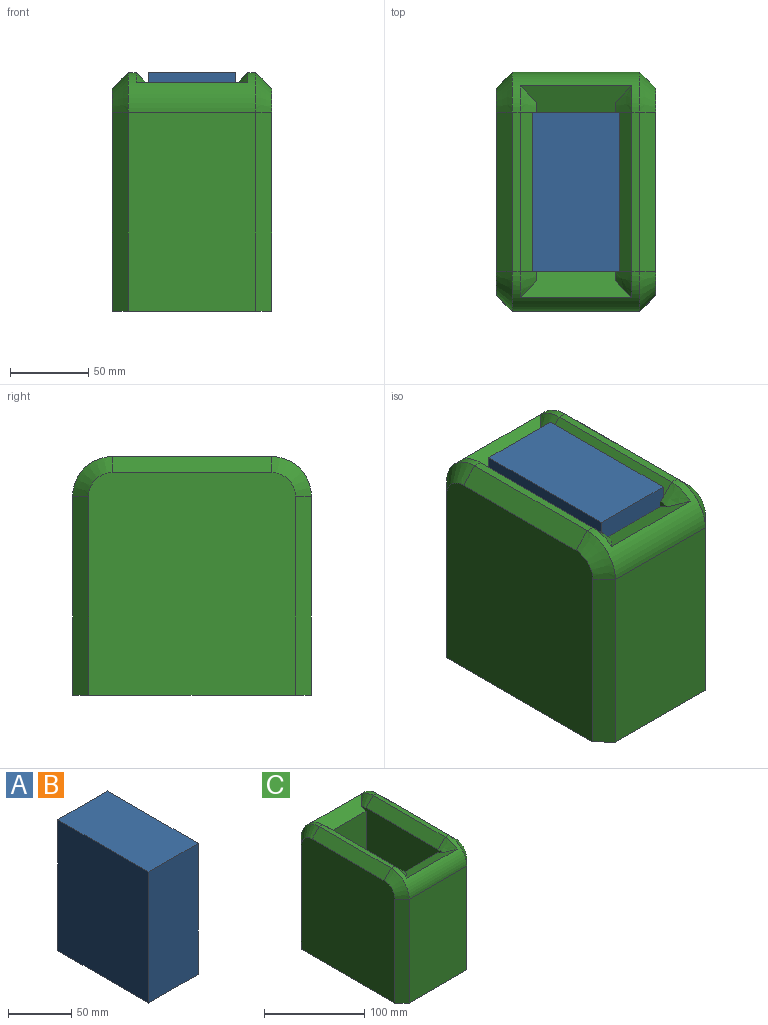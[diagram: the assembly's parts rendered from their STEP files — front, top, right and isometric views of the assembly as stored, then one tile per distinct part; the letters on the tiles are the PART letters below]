
ASSEMBLY  parts=3 mates=1
PART A: 6 faces, bbox 55.7x101.6x127 mm
  f0: plane 127x55.65mm, normal (0,1,0), area 7068mm2, adj f1,f3,f4,f5
  f1: plane 127x101.6mm, normal (-1,0,0), area 12903.2mm2, adj f0,f2,f4,f5
  f2: plane 127x55.65mm, normal (0,-1,0), area 7068mm2, adj f1,f3,f4,f5
  f3: plane 127x101.6mm, normal (1,0,0), area 12903.2mm2, adj f0,f2,f4,f5
  f4: plane 101.6x55.65mm, normal (0,0,1), area 5654.4mm2, adj f0,f1,f2,f3
  f5: plane 101.6x55.65mm, normal (0,0,-1), area 5654.4mm2, adj f0,f1,f2,f3
PART B: same geometry as A
PART C: 32 faces, bbox 101.6x152.4x152.4 mm
  f0: plane 101.6x5.08mm, normal (0,0,1), area 516.1mm2, adj f12,f13,f16,f27
  f1: plane 127x81.28mm, normal (0,1,0), area 10322.6mm2, adj f6,f13,f18,f23
  f2: plane 142.24x132.08mm, normal (-1,0,0), area 18687.4mm2, adj f6,f14,f15,f16,f17,f18
  f3: plane 127x81.28mm, normal (0,-1,0), area 10322.6mm2, adj f6,f12,f14,f19
  f4: plane 142.24x132.08mm, normal (1,0,0), area 18687.4mm2, adj f6,f19,f20,f21,f22,f23
  f5: plane 101.6x5.08mm, normal (0,0,1), area 516.1mm2, adj f12,f13,f21,f28
  f6: plane 152.4x101.6mm, normal (0,0,-1), area 15277.4mm2, adj f1,f2,f3,f4,f14,f18,f19,f23
  f7: plane 116.84x113.52mm, normal (1,0,0), area 11896.6mm2, adj f8,f10,f11,f24,f25,f27,f29,f31
  f8: plane 112.96x50.8mm, normal (0,1,0), area 5738.3mm2, adj f7,f9,f11,f31
  f9: plane 116.84x113.52mm, normal (-1,0,0), area 11896.6mm2, adj f8,f10,f11,f24,f26,f28,f30,f31
  f10: plane 112.96x50.8mm, normal (0,-1,0), area 5738.3mm2, adj f7,f9,f11,f24
  f11: plane 101.6x50.8mm, normal (0,0,1), area 5161.3mm2, adj f7,f8,f9,f10
  f12: cylinder r=25.4mm len=81.28mm, axis (-1,0,0), area 1924.7mm2, adj f0,f3,f5,f15,f20,f29,f30,f31
  f13: cylinder r=25.4mm len=81.28mm, axis (1,0,0), area 1924.7mm2, adj f0,f1,f5,f17,f22,f24,f25,f26
  f14: plane 127x10.16mm, normal (-0.71,-0.71,0), area 1824.8mm2, adj f2,f3,f6,f15
  f15: cone r=15.24mm half-angle=45deg, axis (1,0,0), area 458.6mm2, adj f2,f12,f14,f16
  f16: plane 101.6x10.16mm, normal (-0.71,0,0.71), area 1459.8mm2, adj f0,f2,f15,f17
  f17: cone r=15.24mm half-angle=45deg, axis (1,0,0), area 458.6mm2, adj f2,f13,f16,f18
  f18: plane 127x10.16mm, normal (-0.71,0.71,0), area 1824.8mm2, adj f1,f2,f6,f17
  f19: plane 127x10.16mm, normal (0.71,-0.71,0), area 1824.8mm2, adj f3,f4,f6,f20
  f20: cone r=15.24mm half-angle=45deg, axis (-1,0,0), area 458.6mm2, adj f4,f12,f19,f21
  f21: plane 101.6x10.16mm, normal (0.71,0,0.71), area 1459.8mm2, adj f4,f5,f20,f22
  f22: cone r=15.24mm half-angle=45deg, axis (-1,0,0), area 458.6mm2, adj f4,f13,f21,f23
  f23: plane 127x10.16mm, normal (0.71,0.71,0), area 1824.8mm2, adj f1,f4,f6,f22
  f24: plane 71.12x16.93mm, normal (0,-0.41,0.91), area 1060.3mm2, adj f7,f9,f10,f13,f25,f26
  f25: cone r=15.24mm half-angle=45deg, axis (-1,0,0), area 178.8mm2, adj f7,f13,f24,f27
  f26: cone r=25.4mm half-angle=45deg, axis (1,0,0), area 178.8mm2, adj f9,f13,f24,f28
  f27: plane 101.6x10.16mm, normal (0.71,0,0.71), area 1459.8mm2, adj f0,f7,f25,f29
  f28: plane 101.6x10.16mm, normal (-0.71,0,0.71), area 1459.8mm2, adj f5,f9,f26,f30
  f29: cone r=15.24mm half-angle=45deg, axis (-1,0,0), area 178.8mm2, adj f7,f12,f27,f31
  f30: cone r=25.4mm half-angle=45deg, axis (1,0,0), area 178.8mm2, adj f9,f12,f28,f31
  f31: plane 71.12x16.93mm, normal (0,0.41,0.91), area 1060.3mm2, adj f7,f8,f9,f12,f29,f30
PLACE A t=(-42.05,52.75,47.58)mm
PLACE B t=(-42.05,52.75,47.58)mm
PLACE C t=(-117.05,-39.09,22.18)mm
MATE fastened C.f11 <-> B.f5  axis (0,0,1) through (-67.83,34.89,47.58)mm
